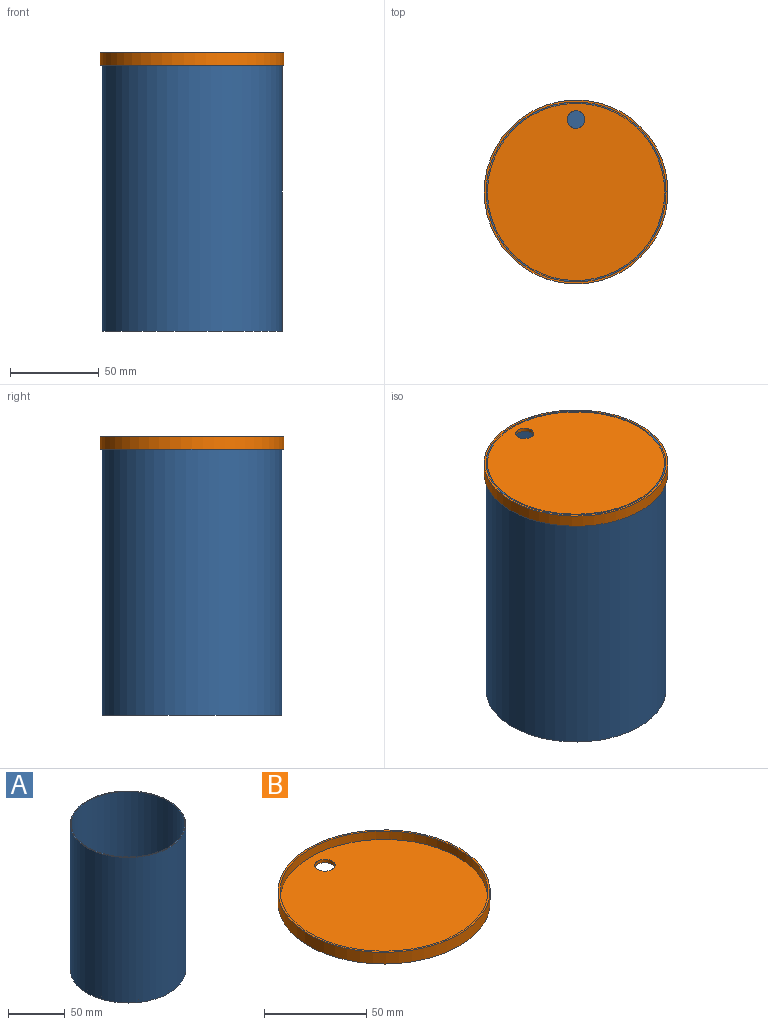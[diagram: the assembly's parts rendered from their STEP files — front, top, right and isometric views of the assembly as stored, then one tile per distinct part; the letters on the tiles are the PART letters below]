
ASSEMBLY  parts=2 mates=1
PART A: 5 faces, bbox 101.6x101.6x157 mm
  f0: cylinder r=50.8mm len=157mm, axis (0,0,-1), area 50112.2mm2, adj f1,f2
  f1: plane 101.6x101.6mm, normal (0,0,1), area 253.3mm2, adj f0,f3
  f2: plane 101.6x101.6mm, normal (0,0,-1), area 8107.3mm2, adj f0
  f3: cylinder r=50mm len=154mm, axis (0,0,1), area 48380.5mm2, adj f1,f4
  f4: plane 100x100mm, normal (0,0,1), area 7854mm2, adj f3
PART B: 6 faces, bbox 103.8x103.8x7 mm
  f0: cylinder r=51.9mm len=103.8mm, axis (0,0,-1), area 2282.7mm2, adj f1,f2
  f1: plane 103.8x103.8mm, normal (0,0,1), area 323mm2, adj f0,f3
  f2: plane 103.8x103.8mm, normal (0,0,-1), area 8383.7mm2, adj f0,f5
  f3: cylinder r=50.9mm len=101.8mm, axis (0,0,1), area 1599.1mm2, adj f1,f4
  f4: plane 101.8x101.8mm, normal (0,0,1), area 8060.7mm2, adj f3,f5
  f5: cylinder r=5mm len=10mm, axis (0,0,-1), area 62.8mm2, adj f2,f4
PLACE A t=(-64.98,-24.04,16.72)mm fixed
PLACE B rot(axis=(0,1,0),180deg) t=(-64.98,-24.04,173.72)mm
MATE fastened B.f0 <-> A.f3  axis (0,0,1) through (-64.98,-24.04,173.72)mm
